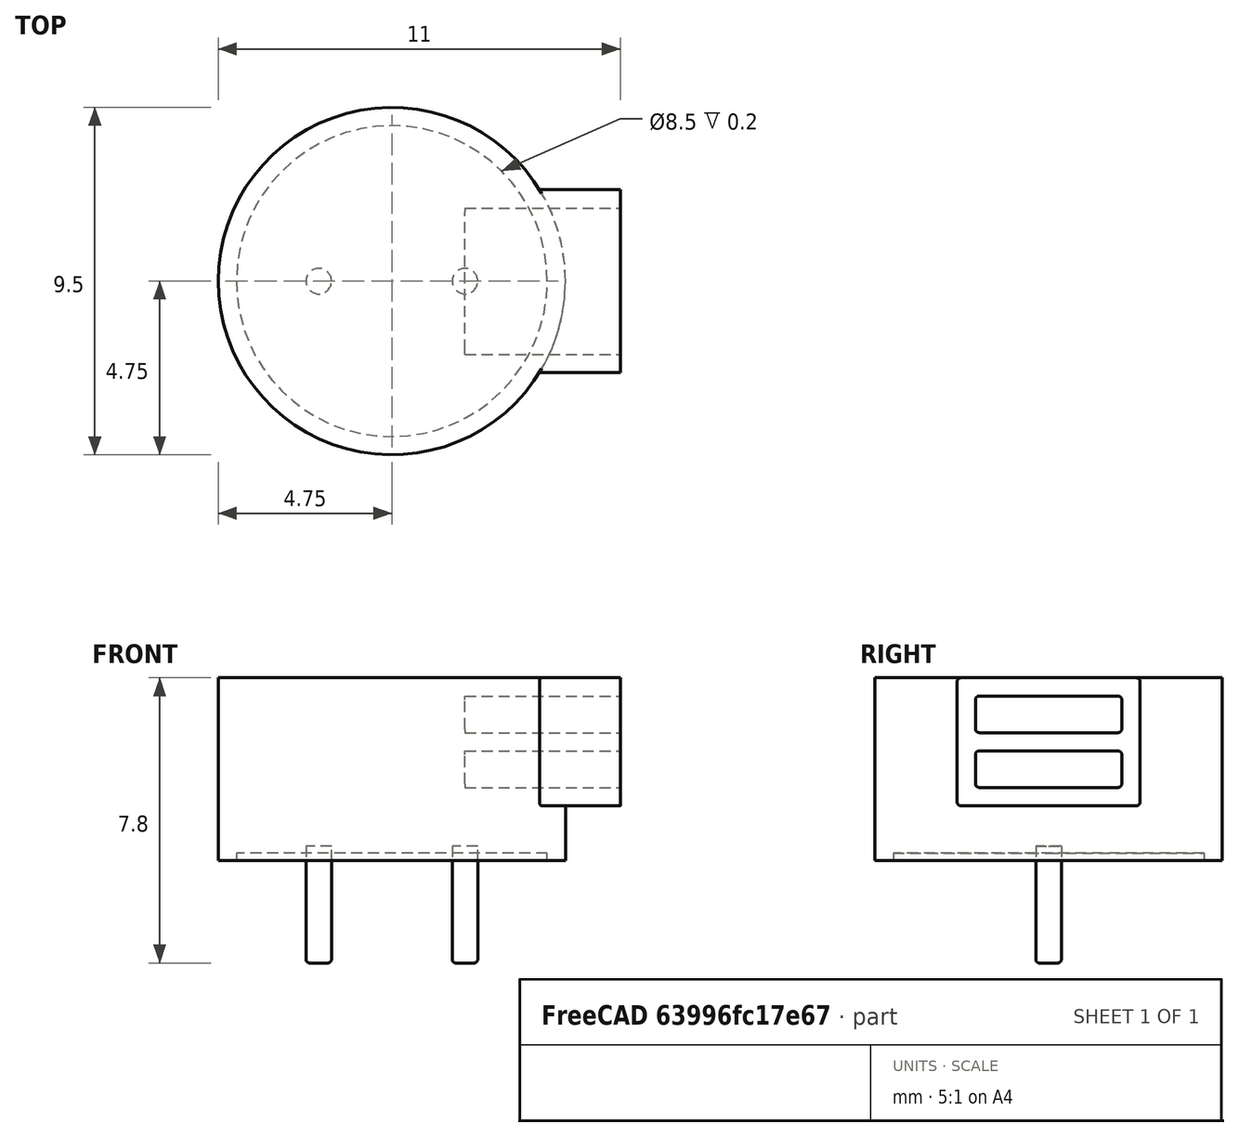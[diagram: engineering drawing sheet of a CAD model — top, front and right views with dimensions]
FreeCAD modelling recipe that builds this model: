
FCSTD DOCUMENT  (FreeCAD 0.20R29410 (Git))
Label: HC09A
License: All rights reserved
LicenseURL: http://en.wikipedia.org/wiki/All_rights_reserved
objects: Part::Fillet×5, Part::Cylinder×4, Part::Box×3, Part::Cut×2, Part::MultiFuse×2
note: 16 computed .brp shape members not serialized (recipe doc carries the construction recipe); baked Part::Feature solids carry a one-line shape summary decoded from their .brp

FEATURE [Part::Cylinder] Cylinder
  Angle = 360
  AttacherType = Attacher::AttachEngine3D
  FirstAngle = 0
  Height = 5
  Radius = 4.75
  SecondAngle = 0
FEATURE [Part::Box] Box  label="Cube"
  AttacherType = Attacher::AttachEngine3D
  Height = 3.5
  Length = 3
  Placement = pos=(3.25,-2.5,1.5) rot=(0,0,1;0rad)
  Width = 5
FEATURE [Part::Fillet] Fillet
  Base = -> Box
  Edges = 4 edges r=0.1: [Edge9,Edge10,Edge11,Edge12]
FEATURE [Part::Box] Box001  label="Cube001"
  AttacherType = Attacher::AttachEngine3D
  Height = 1
  Length = 5
  Placement = pos=(2,-2,2) rot=(0,0,1;0rad)
  Width = 4
FEATURE [Part::Fillet] Fillet001
  Base = -> Box001
  Edges = 4 edges r=0.1: [Edge9,Edge10,Edge11,Edge12]
FEATURE [Part::Box] Box002  label="Cube002"
  AttacherType = Attacher::AttachEngine3D
  Height = 1
  Length = 5
  Placement = pos=(2,-2,2) rot=(0,0,1;0rad)
  Width = 4
FEATURE [Part::Fillet] Fillet002
  Base = -> Box002
  Edges = 4 edges r=0.1: [Edge9,Edge10,Edge11,Edge12]
  Placement = pos=(0,0,1.5) rot=(0,0,1;0rad)
FEATURE [Part::Cylinder] Cylinder001
  Angle = 360
  AttacherType = Attacher::AttachEngine3D
  FirstAngle = 0
  Height = 3.2
  Placement = pos=(2,0,-2.8) rot=(0,0,1;0rad)
  Radius = 0.35
  SecondAngle = 0
FEATURE [Part::Fillet] Fillet003
  Base = -> Cylinder001
  Edges = 1 edges r=0.1: [Edge2]
FEATURE [Part::Cylinder] Cylinder002
  Angle = 360
  AttacherType = Attacher::AttachEngine3D
  FirstAngle = 0
  Height = 0.2
  Radius = 4.25
  SecondAngle = 0
FEATURE [Part::Cut] Cut
  Base = -> Cylinder
  Tool = -> Cylinder002
FEATURE [Part::Cylinder] Cylinder003
  Angle = 360
  AttacherType = Attacher::AttachEngine3D
  FirstAngle = 0
  Height = 3.2
  Placement = pos=(-2,0,-2.8) rot=(0,0,1;0rad)
  Radius = 0.35
  SecondAngle = 0
FEATURE [Part::Fillet] Fillet004
  Base = -> Cylinder003
  Edges = 1 edges r=0.1: [Edge2]
FEATURE [Part::MultiFuse] Fusion
  Shapes = -> [Cut,Fillet]
FEATURE [Part::MultiFuse] Fusion001
  Shapes = -> [Fillet001,Fillet002]
FEATURE [Part::Cut] Cut001
  Base = -> Fusion
  Tool = -> Fusion001
